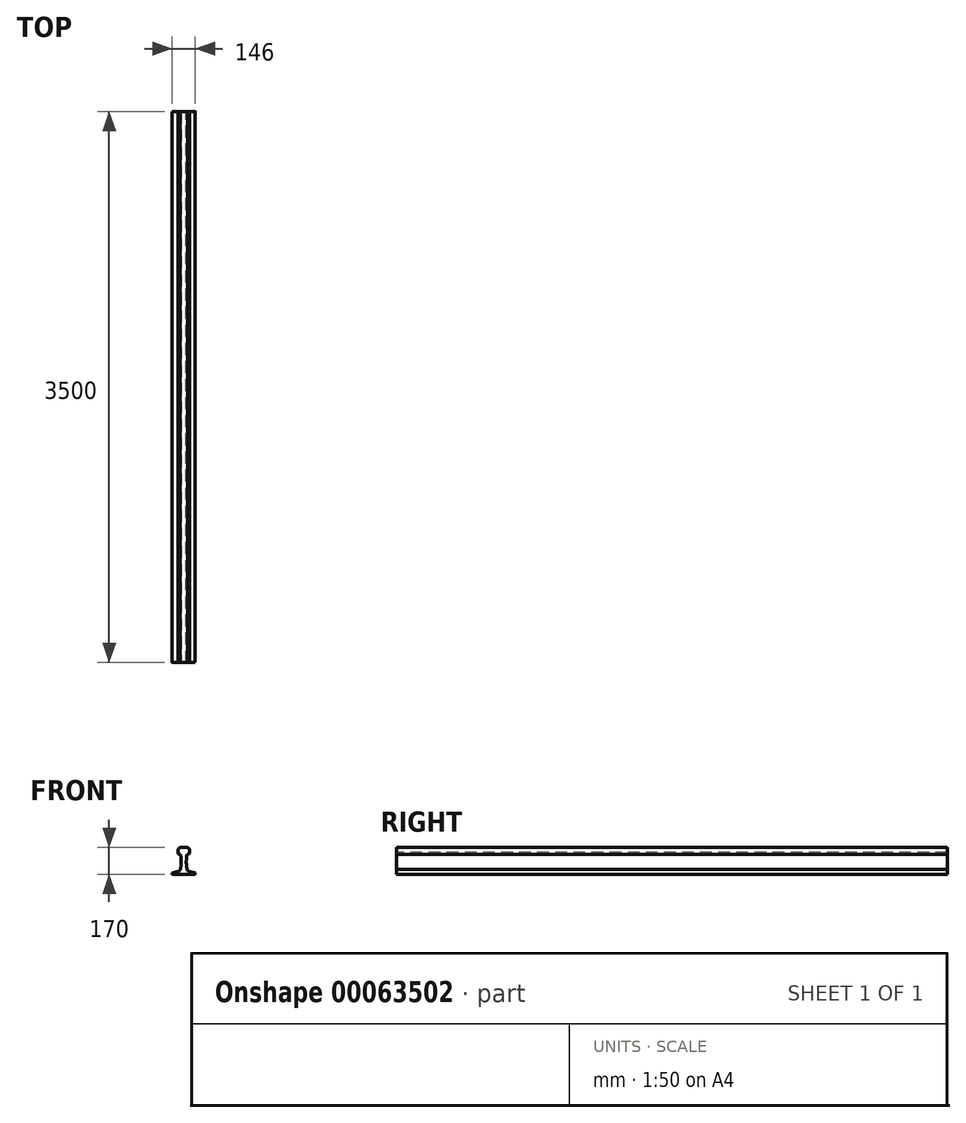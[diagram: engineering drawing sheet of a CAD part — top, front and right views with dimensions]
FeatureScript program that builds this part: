
annotation { "Feature Type Name" : "Feature", "Feature Type Description" : "" }
export const myFeature = defineFeature(function(context is Context, id is Id, definition is map)
    precondition{}
    {
        {
            var Q0;
            Q0=qCreatedBy(makeId("Front.planeOp"),FACE);
            var sketch = newSketch(context, id + "F0", { "sketchPlane" : qUnion([Q0])});
            skLineSegment(sketch, "E0", {"start": v(0, 0) * mm, "end": v(71, 0) * mm});
            skLineSegment(sketch, "E1", {"start": v(0, 0) * mm, "end": v(-71, 0) * mm});
            skLineSegment(sketch, "E2", {"start": v(0, 0) * mm, "end": v(0, 170) * mm, "construction": true});
            skLineSegment(sketch, "E3", {"start": v(-73, 2) * mm, "end": v(-73, 7.4) * mm});
            skArc(sketch, "E4", {"start": v(-73, 2) * mm, "mid": v(-72.41, 0.59) * mm, "end": v(-71, 0) * mm});
            skArc(sketch, "E5", {"start": v(-70.73, 10.32) * mm, "mid": v(-72.36, 9.25) * mm, "end": v(-73, 7.4) * mm});
            skLineSegment(sketch, "E6", {"start": v(73, 2) * mm, "end": v(73, 7.4) * mm});
            skArc(sketch, "E7", {"start": v(71, 0) * mm, "mid": v(72.41, 0.59) * mm, "end": v(73, 2) * mm});
            skArc(sketch, "E8", {"start": v(73, 7.4) * mm, "mid": v(72.36, 9.25) * mm, "end": v(70.73, 10.32) * mm});
            skLineSegment(sketch, "E9", {"start": v(0, 170) * mm, "end": v(-24.05, 170) * mm});
            skLineSegment(sketch, "E10", {"start": v(-35.76, 154.84) * mm, "end": v(-36.44, 141.14) * mm});
            skLineSegment(sketch, "E11.bottom", {"start": v(-24.05, 170) * mm, "end": v(-19, 170) * mm});
            skArc(sketch, "E12", {"start": v(-24.05, 170) * mm, "mid": v(-32.28, 164.25) * mm, "end": v(-35.76, 154.84) * mm});
            skLineSegment(sketch, "E13", {"start": v(-20.05, 126.01) * mm, "end": v(-27.21, 127.8) * mm});
            skLineSegment(sketch, "E14", {"start": v(-36.44, 141.14) * mm, "end": v(-36.56, 138.8) * mm});
            skFitSpline(sketch, "E15", {"points": [v(-36.44, 141.14) * mm, v(-35.26, 131.7) * mm, v(-27.21, 127.8) * mm], "startDerivative": vector(-1.23, -21.29) * mm, "endDerivative": vector(19.8, -5.3) * mm});
            skArc(sketch, "E16", {"start": v(-34.7, 19.32) * mm, "mid": v(-25.9, 24.11) * mm, "end": v(-20.53, 32.58) * mm});
            skLineSegment(sketch, "E17.trimOffspring", {"start": v(-34.7, 19.32) * mm, "end": v(-70.73, 10.32) * mm});
            skPoint(sketch, "E18.orphan", {"position": v(-20.48, 32.71) * mm});
            skPoint(sketch, "E19.end.orphan", {"position": v(-20.48, 32.58) * mm});
            skFitSpline(sketch, "E20", {"points": [v(-20.53, 32.58) * mm, v(-16.85, 65.47) * mm, v(-16.62, 88.53) * mm, v(-18.01, 110.11) * mm, v(-19.64, 123.31) * mm, v(-20.05, 126.01) * mm], "startDerivative": vector(15, 122.65) * mm, "endDerivative": vector(-2.95, 27.62) * mm});
            skLineSegment(sketch, "E21.MirrorCS", {"start": v(0, 170) * mm, "end": v(24.05, 170) * mm});
            skArc(sketch, "E22.MirrorCS", {"start": v(24.05, 170) * mm, "mid": v(32.28, 164.25) * mm, "end": v(35.76, 154.84) * mm});
            skLineSegment(sketch, "E23.MirrorCS", {"start": v(35.76, 154.84) * mm, "end": v(36.44, 141.14) * mm});
            skFitSpline(sketch, "E24.MirrorCS", {"points": [v(36.44, 141.14) * mm, v(35.26, 131.7) * mm, v(27.21, 127.8) * mm], "startDerivative": vector(1.23, -21.29) * mm, "endDerivative": vector(-19.8, -5.3) * mm});
            skLineSegment(sketch, "E25.MirrorCS", {"start": v(20.05, 126.01) * mm, "end": v(27.21, 127.8) * mm});
            skFitSpline(sketch, "E26.MirrorCS", {"points": [v(20.53, 32.58) * mm, v(16.85, 65.47) * mm, v(16.62, 88.53) * mm, v(18.01, 110.11) * mm, v(19.64, 123.31) * mm, v(20.05, 126.01) * mm], "startDerivative": vector(-15, 122.65) * mm, "endDerivative": vector(2.95, 27.62) * mm});
            skArc(sketch, "E27.MirrorCS", {"start": v(34.7, 19.32) * mm, "mid": v(25.9, 24.11) * mm, "end": v(20.53, 32.58) * mm});
            skLineSegment(sketch, "E28.MirrorCS", {"start": v(34.7, 19.32) * mm, "end": v(70.73, 10.32) * mm});
            skSolve(sketch);
        }
        {
            var Q0;
            Q0 = qSketchRegion(id + "F0", true);
            extrude(context, id + "F1", {"entities" : qUnion([Q0]), "depth" : 3500 * mm});
        }
    });
